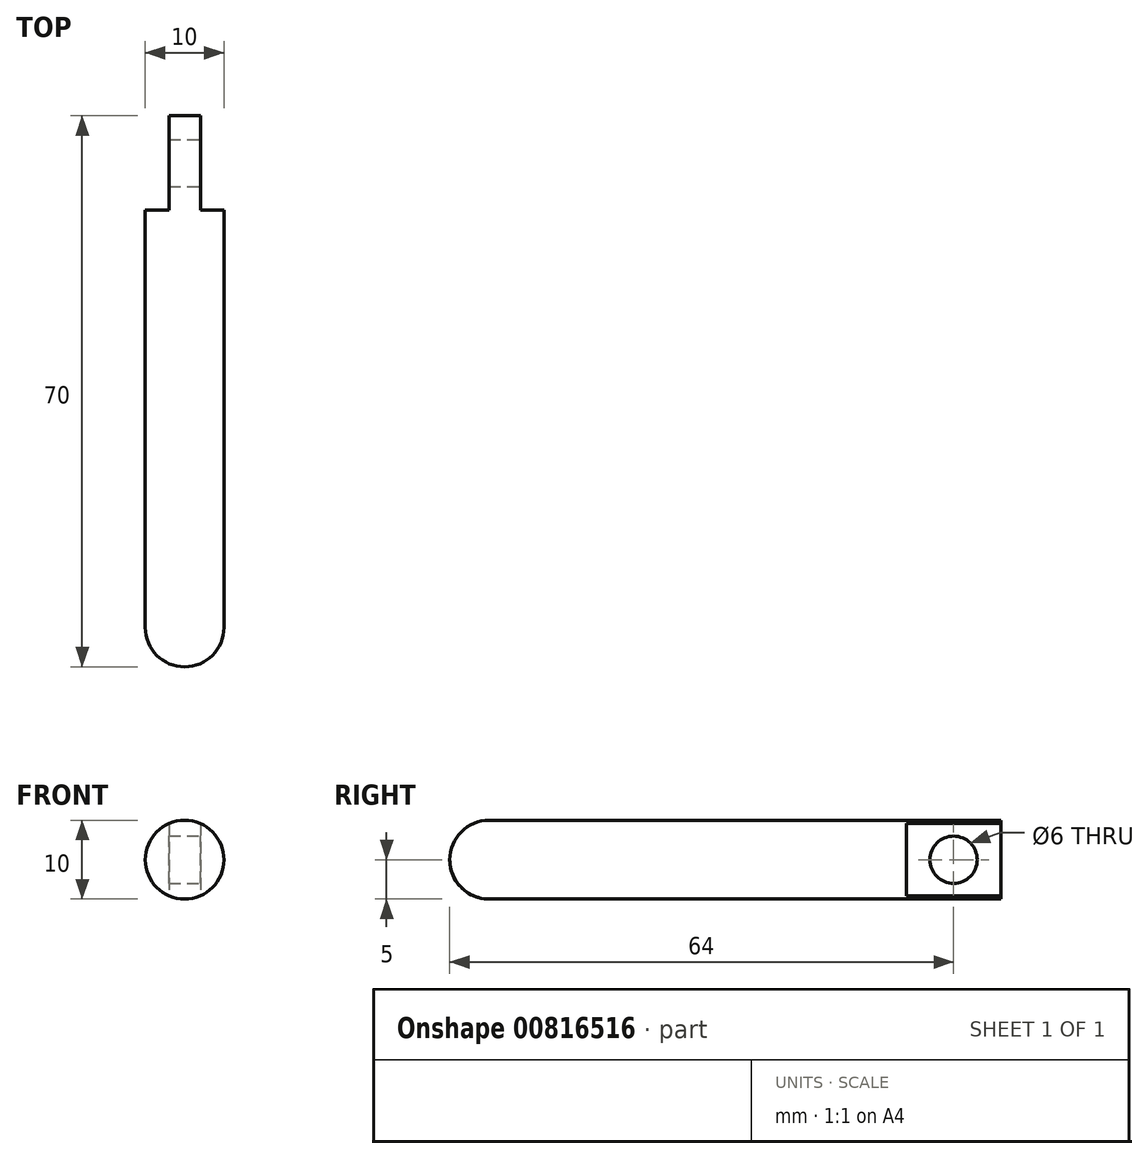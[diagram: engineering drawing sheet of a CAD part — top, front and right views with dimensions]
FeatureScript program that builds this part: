
annotation { "Feature Type Name" : "Feature", "Feature Type Description" : "" }
export const myFeature = defineFeature(function(context is Context, id is Id, definition is map)
    precondition{}
    {
        {
            var Q0;
            Q0=qCreatedBy(makeId("Front.planeOp"),FACE);
            var sketch = newSketch(context, id + "F0", { "sketchPlane" : qUnion([Q0])});
            skCircle(sketch, "E0", {"center": v(0, 0) * mm, "radius": 5 * mm});
            skLineSegment(sketch, "E1", {"start": v(-2, 4.58) * mm, "end": v(-2, -4.58) * mm});
            skLineSegment(sketch, "E2.MirrorCS", {"start": v(2, 4.58) * mm, "end": v(2, -4.58) * mm});
            skPoint(sketch, "E3.orphan", {"position": v(-2, 6.45) * mm});
            skPoint(sketch, "E4.orphan", {"position": v(2, 6.45) * mm});
            skPoint(sketch, "E5.orphan", {"position": v(-2, -7.13) * mm});
            skPoint(sketch, "E6.orphan", {"position": v(2, -7.13) * mm});
            skSolve(sketch);
        }
        {
            var Q0;
            Q0=qSketchRegion(id+"F0",true);
            extrude(context, id + "F1", {"entities" : qUnion([Q0]), "depth" : 70 * mm, "offsetDistance" : 25 * mm});
        }
        {
            var Q0;
            {var subQ0=sQuery(id+"F0.wireOp",EDGE,"E1");Q0=makeQuery(id+"F0.imprint","IMPRINT",FACE,{"disambiguationData":[TD([[makeQuery(id+"F0.imprint","IMPRINT",EDGE,{"derivedFrom":subQ0}),-1.0]])]});}
            var Q1;
            {var subQ0=sQuery(id+"F0.wireOp",EDGE,"E2.MirrorCS");Q1=makeQuery(id+"F0.imprint","IMPRINT",FACE,{"disambiguationData":[TD([[makeQuery(id+"F0.imprint","IMPRINT",EDGE,{"derivedFrom":subQ0}),1.0]])]});}
            extrude(context, id + "F2", {"entities" : qUnion([Q0, Q1]), "operationType" : NewBodyOperationType.REMOVE, "depth" : 12 * mm, "offsetDistance" : 25 * mm});
        }
        {
            var Q0;
            Q0=makeQuery(id+"F2.boolean.opBoolean","COPY",FACE,{"derivedFrom":makeQuery(id+"F2.opExtrude","SWEPT_FACE",FACE,{"disambiguationData":[OSD([sQuery(id+"F0.wireOp",EDGE,"E2.MirrorCS")])]})});
            var sketch = newSketch(context, id + "F3", { "sketchPlane" : qUnion([Q0])});
            skCircle(sketch, "E7", {"center": v(-6, 0) * mm, "radius": 3 * mm});
            skSolve(sketch);
        }
        {
            var Q0;
            Q0=makeQuery(id+"F3.imprint","IMPRINT",FACE,{"disambiguationData":[TD([[makeQuery(id+"F3.imprint","IMPRINT",EDGE,{"derivedFrom":sQuery(id+"F3.wireOp",EDGE,"E7")}),1.0]])]});
            extrude(context, id + "F4", {"entities" : qUnion([Q0]), "operationType" : NewBodyOperationType.REMOVE, "oppositeDirection" : true, "depth" : 25 * mm, "offsetDistance" : 25 * mm});
        }
        {
            var Q0;
            Q0=makeQuery(id+"F1.opExtrude","CAP_EDGE",EDGE,{"disambiguationData":[OSD([sQuery(id+"F0.wireOp",EDGE,"E0")])],"isStart":false});
            fillet(context, id + "F5", {"entities" : qUnion([Q0]), "radius" : 5 * mm, "tangentPropagation" : true, "allowEdgeOverflow" : false});
        }
    });
